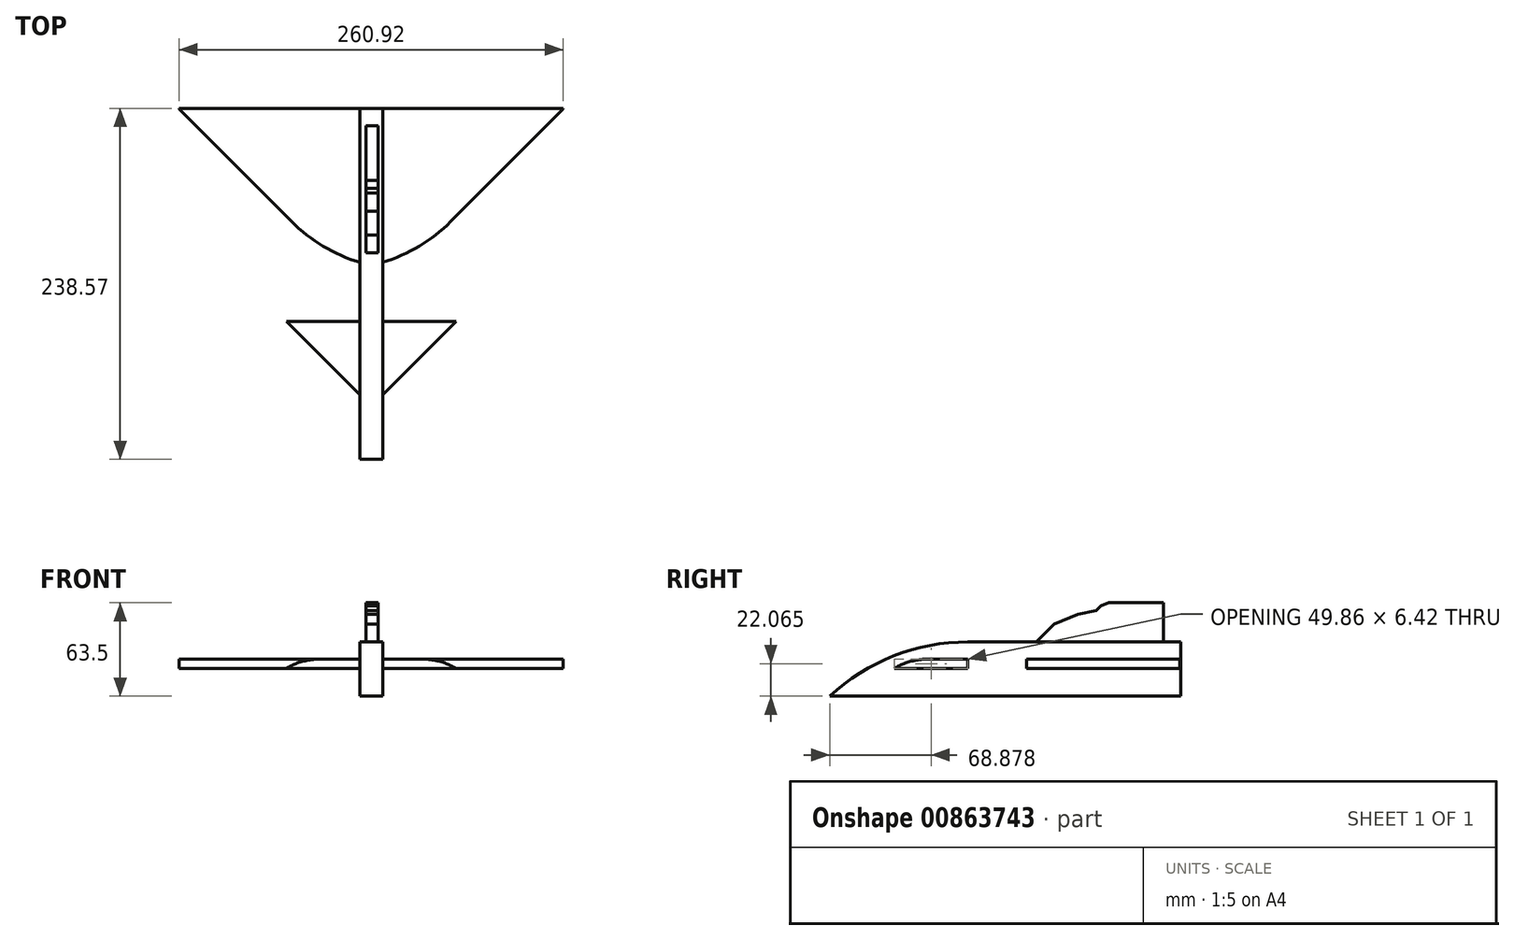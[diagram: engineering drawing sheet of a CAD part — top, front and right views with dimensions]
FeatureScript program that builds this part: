
annotation { "Feature Type Name" : "Feature", "Feature Type Description" : "" }
export const myFeature = defineFeature(function(context is Context, id is Id, definition is map)
    precondition{}
    {
        {
            var Q0;
            Q0=qCreatedBy(makeId("Top.planeOp"),FACE);
            var sketch = newSketch(context, id + "F0", { "sketchPlane" : qUnion([Q0])});
            skLineSegment(sketch, "E0.bottom", {"start": v(7.78, 119.92) * mm, "end": v(-7.78, 119.92) * mm});
            skLineSegment(sketch, "E0.top", {"start": v(7.78, -119.92) * mm, "end": v(-7.78, -119.92) * mm});
            skLineSegment(sketch, "E0.left", {"start": v(7.78, 119.92) * mm, "end": v(7.78, -119.92) * mm});
            skLineSegment(sketch, "E0.right", {"start": v(-7.78, 119.92) * mm, "end": v(-7.78, -119.92) * mm});
            skPoint(sketch, "E0.middle", {"position": v(0, 0) * mm});
            skSolve(sketch);
        }
        {
            var Q0;
            Q0 = qSketchRegion(id + "F0", true);
            extrude(context, id + "F1", {"entities" : qUnion([Q0]), "depth" : 36.83 * mm, "offsetDistance" : 25.4 * mm});
        }
        {
            var Q0;
            Q0=makeQuery(id+"F1.opExtrude","CAP_EDGE",EDGE,{"disambiguationData":[OSD([sQuery(id+"F0.wireOp",EDGE,"E0.top")])],"isStart":false});
            chamfer(context, id + "F2", {"entities" : qUnion([Q0]), "width" : 38.1 * mm, "tangentPropagation" : true});
        }
        {
            var Q0;
            Q0=makeQuery(id+"F1.opExtrude","SWEPT_FACE",FACE,{"disambiguationData":[OSD([sQuery(id+"F0.wireOp",EDGE,"E0.right")])]});
            var sketch = newSketch(context, id + "F3", { "sketchPlane" : qUnion([Q0])});
            skLineSegment(sketch, "E1.bottom", {"start": v(74.7, 18.85) * mm, "end": v(24.84, 18.85) * mm});
            skLineSegment(sketch, "E1.top", {"start": v(74.7, 25.28) * mm, "end": v(24.84, 25.28) * mm});
            skLineSegment(sketch, "E1.left", {"start": v(74.7, 18.85) * mm, "end": v(74.7, 25.28) * mm});
            skLineSegment(sketch, "E1.right", {"start": v(24.84, 18.85) * mm, "end": v(24.84, 25.28) * mm});
            skPoint(sketch, "E1.middle", {"position": v(49.77, 22.07) * mm});
            skSolve(sketch);
        }
        {
            var Q0;
            Q0 = qSketchRegion(id + "F3", true);
            extrude(context, id + "F4", {"entities" : qUnion([Q0]), "operationType" : NewBodyOperationType.ADD, "depth" : 50.8 * mm, "offsetDistance" : 25.4 * mm});
        }
        {
            var Q0;
            Q0=makeQuery(id+"F1.opExtrude","SWEPT_FACE",FACE,{"disambiguationData":[OSD([sQuery(id+"F0.wireOp",EDGE,"E0.right")])]});
            var sketch = newSketch(context, id + "F5", { "sketchPlane" : qUnion([Q0])});
            skPoint(sketch, "E2.centerSnap0", {"position": v(74.7, 22.07) * mm});
            skLineSegment(sketch, "E3.bottom", {"start": v(-15.22, 25.28) * mm, "end": v(-119.92, 25.28) * mm});
            skLineSegment(sketch, "E3.top", {"start": v(-15.22, 18.85) * mm, "end": v(-119.92, 18.85) * mm});
            skLineSegment(sketch, "E3.left", {"start": v(-15.22, 25.28) * mm, "end": v(-15.22, 18.85) * mm});
            skLineSegment(sketch, "E3.right", {"start": v(-119.92, 25.28) * mm, "end": v(-119.92, 18.85) * mm});
            skSolve(sketch);
        }
        {
            var Q0;
            {var subQ0=sQuery(id+"F0.wireOp",EDGE,"E0.top");Q0=makeQuery(id+"F2.opChamfer","BLEND_EDGE",EDGE,{"blendedFrom":[makeQuery(id+"F1.opExtrude","CAP_EDGE",EDGE,{"disambiguationData":[OSD([subQ0])],"isStart":false}),makeQuery(id+"F1.opExtrude","CAP_FACE",FACE,{"disambiguationData":[OSD([sQuery(id+"F0.wireOp",EDGE,"E0.bottom"),subQ0,sQuery(id+"F0.wireOp",EDGE,"E0.left"),sQuery(id+"F0.wireOp",EDGE,"E0.right")])],"isStart":false})],"blendedInto":[makeQuery(id+"F1.opExtrude","CAP_FACE",FACE,{"disambiguationData":[OSD([sQuery(id+"F0.wireOp",EDGE,"E0.bottom"),subQ0,sQuery(id+"F0.wireOp",EDGE,"E0.left"),sQuery(id+"F0.wireOp",EDGE,"E0.right")])],"isStart":false})]});}
            fillet(context, id + "F6", {"entities" : qUnion([Q0]), "radius" : 137.8 * mm, "tangentPropagation" : true, "allowEdgeOverflow" : false});
        }
        {
            var Q0;
            Q0=makeQuery(id+"F4.opExtrude","CAP_EDGE",EDGE,{"disambiguationData":[OSD([sQuery(id+"F3.wireOp",EDGE,"E1.left")])],"isStart":false});
            chamfer(context, id + "F7", {"entities" : qUnion([Q0]), "width" : 50.8 * mm, "tangentPropagation" : true});
        }
        {
            var Q0;
            Q0=makeQuery(id+"F7.opChamfer","BLEND_EDGE",EDGE,{"blendedFrom":[makeQuery(id+"F4.opExtrude","CAP_EDGE",EDGE,{"disambiguationData":[OSD([sQuery(id+"F3.wireOp",EDGE,"E1.left")])],"isStart":false}),makeQuery(id+"F4.opExtrude","SWEPT_FACE",FACE,{"disambiguationData":[OSD([sQuery(id+"F3.wireOp",EDGE,"E1.top")])]})],"blendedInto":[makeQuery(id+"F4.opExtrude","SWEPT_FACE",FACE,{"disambiguationData":[OSD([sQuery(id+"F3.wireOp",EDGE,"E1.top")])]})]});
            fillet(context, id + "F8", {"entities" : qUnion([Q0]), "radius" : 25.4 * mm, "tangentPropagation" : true, "allowEdgeOverflow" : false});
        }
        {
            var Q0;
            Q0 = qSketchRegion(id + "F5", true);
            extrude(context, id + "F9", {"entities" : qUnion([Q0]), "operationType" : NewBodyOperationType.ADD, "depth" : 122.68 * mm, "offsetDistance" : 25.4 * mm});
        }
        {
            var Q0;
            Q0=makeQuery(id+"F9.opExtrude","CAP_EDGE",EDGE,{"disambiguationData":[OSD([sQuery(id+"F5.wireOp",EDGE,"E3.left")])],"isStart":false});
            chamfer(context, id + "F10", {"entities" : qUnion([Q0]), "width" : 104.14 * mm, "tangentPropagation" : true});
        }
        {
            var Q0;
            {var subQ0=sQuery(id+"F5.wireOp",EDGE,"E3.left");Q0=makeQuery(id+"F10.opChamfer","BLEND_EDGE",EDGE,{"blendedFrom":[makeQuery(id+"F9.opExtrude","CAP_EDGE",EDGE,{"disambiguationData":[OSD([subQ0])],"isStart":false}),makeQuery(id+"F9.opExtrude","SWEPT_FACE",FACE,{"disambiguationData":[OSD([subQ0])]})],"blendedInto":[makeQuery(id+"F9.opExtrude","SWEPT_FACE",FACE,{"disambiguationData":[OSD([subQ0])]})]});}
            fillet(context, id + "F11", {"entities" : qUnion([Q0]), "radius" : 110.98 * mm, "tangentPropagation" : true, "allowEdgeOverflow" : false});
        }
        {
            var Q0;
            Q0=makeQuery(id+"F1.opExtrude","SWEPT_BODY",BODY,{"disambiguationData":[OSD([sQuery(id+"F0.wireOp",EDGE,"E0.bottom"),sQuery(id+"F0.wireOp",EDGE,"E0.top"),sQuery(id+"F0.wireOp",EDGE,"E0.left"),sQuery(id+"F0.wireOp",EDGE,"E0.right")])]});
            var Q1;
            Q1=qCreatedBy(makeId("Right.planeOp"),FACE);
            mirror(context, id + "F12", {"operationType" : NewBodyOperationType.ADD, "entities" : qUnion([Q0]), "mirrorPlane" : qUnion([Q1])});
        }
        {
            var Q0;
            Q0=makeQuery(id+"F1.opExtrude","CAP_FACE",FACE,{"disambiguationData":[OSD([sQuery(id+"F0.wireOp",EDGE,"E0.bottom"),sQuery(id+"F0.wireOp",EDGE,"E0.top"),sQuery(id+"F0.wireOp",EDGE,"E0.left"),sQuery(id+"F0.wireOp",EDGE,"E0.right")])],"isStart":false});
            var sketch = newSketch(context, id + "F13", { "sketchPlane" : qUnion([Q0])});
            skLineSegment(sketch, "E4.bottom", {"start": v(-3.41, 6.55) * mm, "end": v(4.62, 6.55) * mm});
            skLineSegment(sketch, "E4.top", {"start": v(-3.41, 108.08) * mm, "end": v(4.62, 108.08) * mm});
            skLineSegment(sketch, "E4.left", {"start": v(-3.41, 6.55) * mm, "end": v(-3.41, 108.08) * mm});
            skLineSegment(sketch, "E4.right", {"start": v(4.62, 6.55) * mm, "end": v(4.62, 108.08) * mm});
            skSolve(sketch);
        }
        {
            var Q0;
            Q0=makeQuery(id+"F13.imprint","IMPRINT",FACE,{"disambiguationData":[TD([[makeQuery(id+"F13.imprint","IMPRINT",EDGE,{"derivedFrom":sQuery(id+"F13.wireOp",EDGE,"E4.bottom")}),1.0]])]});
            extrude(context, id + "F14", {"entities" : qUnion([Q0]), "operationType" : NewBodyOperationType.ADD, "depth" : 20.32 * mm, "offsetDistance" : 25.4 * mm});
        }
        {
            var Q0;
            Q0=makeQuery(id+"F14.opExtrude","CAP_EDGE",EDGE,{"disambiguationData":[OSD([sQuery(id+"F13.wireOp",EDGE,"E4.bottom")])],"isStart":false});
            chamfer(context, id + "F15", {"entities" : qUnion([Q0]), "width" : 35.56 * mm, "tangentPropagation" : true});
        }
        {
            var Q0;
            {var subQ0=sQuery(id+"F13.wireOp",EDGE,"E4.bottom");Q0=makeQuery(id+"F15.opChamfer","BLEND_EDGE",EDGE,{"blendedFrom":[makeQuery(id+"F14.opExtrude","CAP_EDGE",EDGE,{"disambiguationData":[OSD([subQ0])],"isStart":false}),makeQuery(id+"F14.opExtrude","CAP_FACE",FACE,{"disambiguationData":[OSD([subQ0,sQuery(id+"F13.wireOp",EDGE,"E4.top"),sQuery(id+"F13.wireOp",EDGE,"E4.left"),sQuery(id+"F13.wireOp",EDGE,"E4.right")])],"isStart":false})],"blendedInto":[makeQuery(id+"F14.opExtrude","CAP_FACE",FACE,{"disambiguationData":[OSD([subQ0,sQuery(id+"F13.wireOp",EDGE,"E4.top"),sQuery(id+"F13.wireOp",EDGE,"E4.left"),sQuery(id+"F13.wireOp",EDGE,"E4.right")])],"isStart":false})]});}
            chamfer(context, id + "F16", {"entities" : qUnion([Q0]), "width" : 27.94 * mm, "tangentPropagation" : true});
        }
        {
            var Q0;
            {var subQ0=sQuery(id+"F13.wireOp",EDGE,"E4.bottom");var subQ1=makeQuery(id+"F14.opExtrude","CAP_FACE",FACE,{"disambiguationData":[OSD([subQ0,sQuery(id+"F13.wireOp",EDGE,"E4.top"),sQuery(id+"F13.wireOp",EDGE,"E4.left"),sQuery(id+"F13.wireOp",EDGE,"E4.right")])],"isStart":false});Q0=makeQuery(id+"F16.opChamfer","BLEND_EDGE",EDGE,{"blendedFrom":[makeQuery(id+"F15.opChamfer","BLEND_EDGE",EDGE,{"blendedFrom":[makeQuery(id+"F14.opExtrude","CAP_EDGE",EDGE,{"disambiguationData":[OSD([subQ0])],"isStart":false}),subQ1],"blendedInto":[subQ1]}),subQ1],"blendedInto":[subQ1]});}
            chamfer(context, id + "F17", {"entities" : qUnion([Q0]), "width" : 20.32 * mm, "tangentPropagation" : true});
        }
        {
            var Q0;
            Q0=makeQuery(id+"F14.opExtrude","CAP_FACE",FACE,{"disambiguationData":[OSD([sQuery(id+"F13.wireOp",EDGE,"E4.bottom"),sQuery(id+"F13.wireOp",EDGE,"E4.top"),sQuery(id+"F13.wireOp",EDGE,"E4.left"),sQuery(id+"F13.wireOp",EDGE,"E4.right")])],"isStart":false});
            extrude(context, id + "F18", {"entities" : qUnion([Q0]), "operationType" : NewBodyOperationType.ADD, "depth" : 6.35 * mm, "offsetDistance" : 25.4 * mm});
        }
        {
            var Q0;
            Q0=makeQuery(id+"F18.opExtrude","CAP_EDGE",EDGE,{"disambiguationData":[OSD([sQuery(id+"F13.wireOp",EDGE,"E4.bottom"),sQuery(id+"F13.wireOp",EDGE,"E4.top"),sQuery(id+"F13.wireOp",EDGE,"E4.left"),sQuery(id+"F13.wireOp",EDGE,"E4.right")])],"isStart":false});
            chamfer(context, id + "F19", {"entities" : qUnion([Q0]), "width" : 10.16 * mm, "tangentPropagation" : true});
        }
        {
            var Q0;
            {var subQ0=sQuery(id+"F13.wireOp",EDGE,"E4.right");var subQ1=sQuery(id+"F13.wireOp",EDGE,"E4.left");var subQ2=sQuery(id+"F13.wireOp",EDGE,"E4.top");var subQ3=sQuery(id+"F13.wireOp",EDGE,"E4.bottom");Q0=makeQuery(id+"F19.opChamfer","BLEND_EDGE",EDGE,{"blendedFrom":[makeQuery(id+"F18.opExtrude","CAP_EDGE",EDGE,{"disambiguationData":[OSD([subQ3,subQ2,subQ1,subQ0])],"isStart":false}),makeQuery(id+"F18.opExtrude","CAP_FACE",FACE,{"disambiguationData":[OSD([subQ3,subQ2,subQ1,subQ0])],"isStart":false})],"blendedInto":[makeQuery(id+"F18.opExtrude","CAP_FACE",FACE,{"disambiguationData":[OSD([subQ3,subQ2,subQ1,subQ0])],"isStart":false})]});}
            chamfer(context, id + "F20", {"entities" : qUnion([Q0]), "width" : 7.62 * mm, "tangentPropagation" : true});
        }
    });
